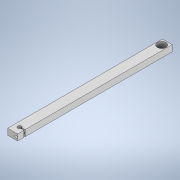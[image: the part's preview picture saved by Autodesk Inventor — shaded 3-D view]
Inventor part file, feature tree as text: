
AUTODESK INVENTOR PART (.ipt)
format: ipt  version: 2021.3 (Build 253353000, 353)  size: 148,480 bytes
history: native  units: mm
features: sketch x7, extrude x4, hole x3
ambient origin geometry x8: Origin, YZ Plane, XZ Plane, XY Plane, X Axis, Y Axis, Z Axis, Center Point
bodies: Volumenkörper1 (feature_tree)
feature tree (14):
  extrude  "Extrusion1"  Depth=250.0mm
  extrude  "Extrusion2"  Depth=2.0mm
  hole  "Bohrung1"  [1 undecoded]
  hole  "Bohrung2"  [1 undecoded]
  extrude  "Extrusion3"  Depth=2.0mm
  extrude  "Extrusion4"  Depth=2.0mm
  hole  "Bohrung4"  [1 undecoded]
  sketch  "Skizze2"  dims[d0=16.0mm d1=250.0mm]
  sketch  "Skizze3"  dims[d2=10.0mm d3=0.0mm d4=2.0mm]
  sketch  "Skizze4"  dims[d5=10.0mm d6=7.5mm d7=0.0mm]
  sketch  "Skizze5"  dims[d8=5.0mm d9=2.5mm]
  sketch  "Skizze7"  dims[d10=4.2mm d11=17.0mm d12=4.0mm d13=2.0mm d14=90.0deg d15=18.0mm d16=20.594885mm d17=11.0mm]
  sketch  "Skizze9"  dims[d18=8.0mm]
  sketch  "Skizze10"  dims[d19=6.0mm d20=17.0mm d21=4.0mm d22=2.0mm d23=90.0deg d24=18.0mm d25=20.594885mm d35=14.1mm d36=8.0mm d38=9.0mm d39=0.0mm d40=12.1mm d41=0.0mm d42=0.0mm d43=230.0mm d47=3.242mm d48=18.0mm d49=4.0mm d50=2.0mm d51=90.0deg d52=18.0mm d53=20.594885mm d54=0.75mm d55=20.594885mm d56=0.0625mm d57=0.75mm d58=0.375mm]
note: 3 required parameter values undecoded (feature->parameter linkage not recoverable at this tier; creation-order binding heuristic only, values carry confidence <= 0.55)
